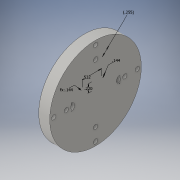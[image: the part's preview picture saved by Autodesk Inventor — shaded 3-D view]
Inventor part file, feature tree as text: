
AUTODESK INVENTOR PART (.ipt)
format: ipt  version: 2016 (Build 200138000, 138)  size: 182,272 bytes
history: native  units: in
note: dims shown in document units (in); Inventor stores cm internally (conversion verified against a paired STEP export)
features: sketch x7, extrude x3, revolve x1
ambient origin geometry x8: Origin, YZ Plane, XZ Plane, XY Plane, X Axis, Y Axis, Z Axis, Center Point
bodies: Solid1 (feature_tree)
feature tree (11):
  revolve  "Revolution1"  [1 undecoded]
  extrude  "Extrusion1"  Depth=0.105in
  sketch  "Sketch3"  dims[d4=0.105in d5=0.255in]
  sketch  "Sketch4"  dims[d6=0.2in d7=0.1in]
  extrude  "Extrusion2"  Depth=0.105in
  sketch  "Sketch5"  dims[d8=90.0deg]
  extrude  "Extrusion3"  Depth=0.1in
  sketch  "Sketch7"  dims[d10=1.5748in d12=360.0deg d14=0.5in d15=0.0in d16=0.255in d17=0.1275in d18=0.1181in d19=1.5748in d21=360.0deg d23=0.2in d24=0.0in d25=1.14in d26=0.787in d27=0.2in d28=0.2in d29=0.5in d30=0.0in d31=0.144in d32=0.144in d33=0.532in d34=0.22in]
  sketch  "Sketch1"  dims[d0=1.2499in d1=0.3in]
  sketch  "Sketch2"  dims[d2=0.22in d3=0.105in]
  sketch  "Sketch6"  dims[d9=0.1181in]
note: 1 required parameter value undecoded (feature->parameter linkage not recoverable at this tier; creation-order binding heuristic only, values carry confidence <= 0.55)
